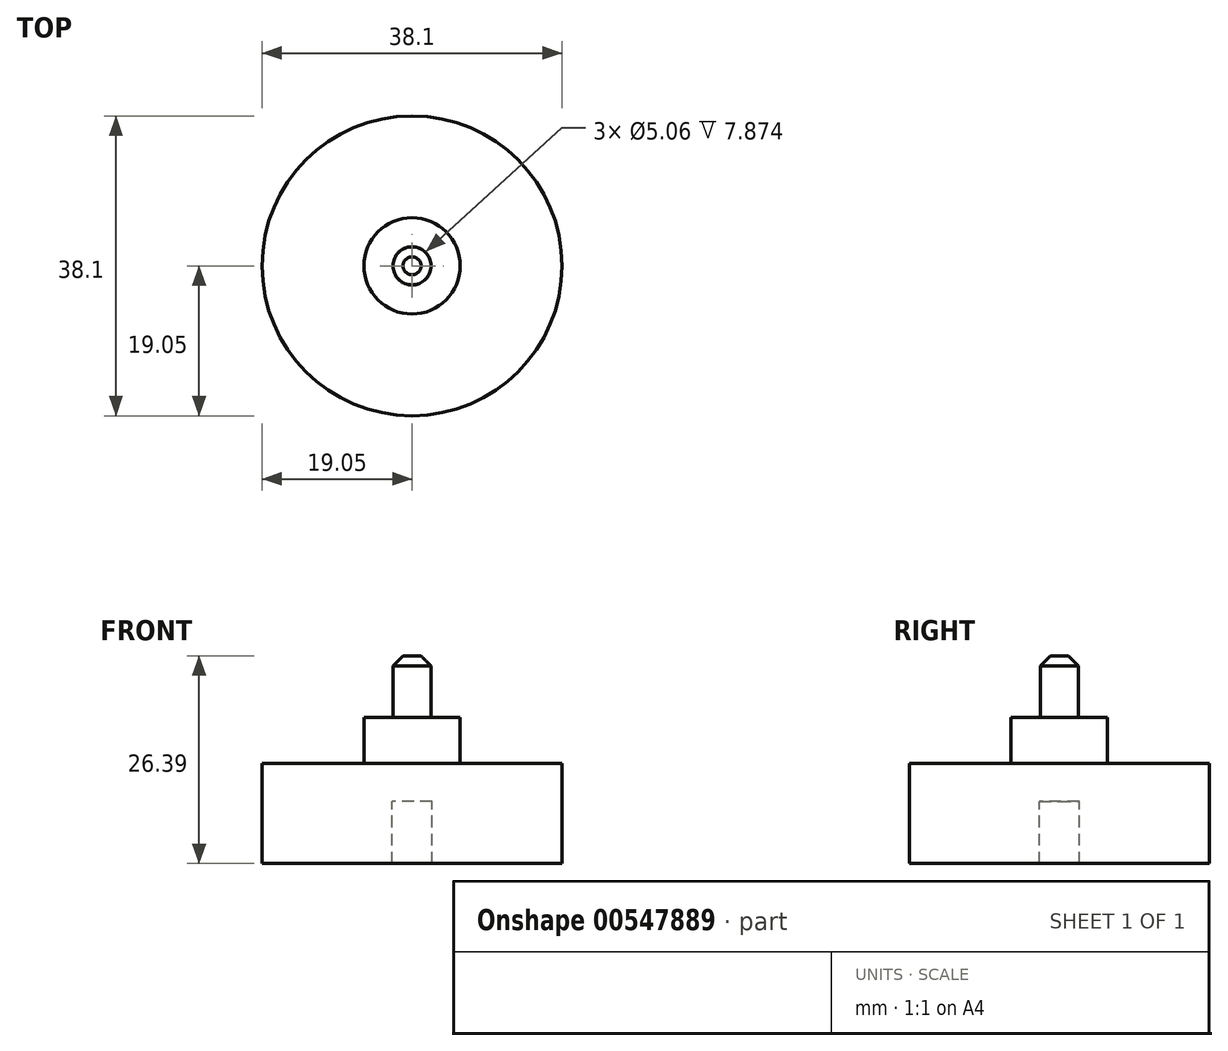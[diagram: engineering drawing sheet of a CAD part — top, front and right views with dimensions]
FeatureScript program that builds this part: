
annotation { "Feature Type Name" : "Feature", "Feature Type Description" : "" }
export const myFeature = defineFeature(function(context is Context, id is Id, definition is map)
    precondition{}
    {
        {
            var Q0;
            Q0=qCreatedBy(makeId("Front.planeOp"),FACE);
            var sketch = newSketch(context, id + "F0", { "sketchPlane" : qUnion([Q0])});
            skLineSegment(sketch, "E0", {"start": v(19.05, 0) * mm, "end": v(19.05, 12.7) * mm});
            skLineSegment(sketch, "E1", {"start": v(6.12, 18.54) * mm, "end": v(6.12, 12.7) * mm});
            skLineSegment(sketch, "E2", {"start": v(19.05, 12.7) * mm, "end": v(6.12, 12.7) * mm});
            skLineSegment(sketch, "E3", {"start": v(2.53, 0) * mm, "end": v(2.53, 7.87) * mm});
            skLineSegment(sketch, "E4", {"start": v(2.53, 7.87) * mm, "end": v(0, 7.87) * mm});
            skLineSegment(sketch, "E5", {"start": v(19.05, 0) * mm, "end": v(2.53, 0) * mm});
            skLineSegment(sketch, "E6", {"start": v(0, 26.4) * mm, "end": v(0, 7.87) * mm});
            skLineSegment(sketch, "E7", {"start": v(0, 26.4) * mm, "end": v(2.41, 26.4) * mm});
            skLineSegment(sketch, "E8", {"start": v(2.41, 26.4) * mm, "end": v(2.41, 18.54) * mm});
            skLineSegment(sketch, "E9", {"start": v(6.12, 18.54) * mm, "end": v(2.41, 18.54) * mm});
            skSolve(sketch);
        }
        {
            var Q0;
            Q0=makeQuery(id+"F0.imprint","IMPRINT",FACE,{"disambiguationData":[TD([[makeQuery(id+"F0.imprint","IMPRINT",EDGE,{"derivedFrom":sQuery(id+"F0.wireOp",EDGE,"E0")}),1.0]])]});
            var Q1;
            Q1=sQuery(id+"F0.wireOp",EDGE,"E6");
            revolve(context, id + "F1", {"entities" : qUnion([Q0]), "axis" : qUnion([Q1]), "revolveType" : RevolveType.FULL});
        }
        {
            var Q0;
            Q0=makeQuery(id+"F1.opRevolve","SWEPT_EDGE",EDGE,{"disambiguationData":[OSD([sQuery(id+"F0.wireOp",EDGE,"E7"),sQuery(id+"F0.wireOp",EDGE,"E8")])]});
            chamfer(context, id + "F2", {"entities" : qUnion([Q0]), "width" : 1.27 * mm, "tangentPropagation" : true});
        }
    });
